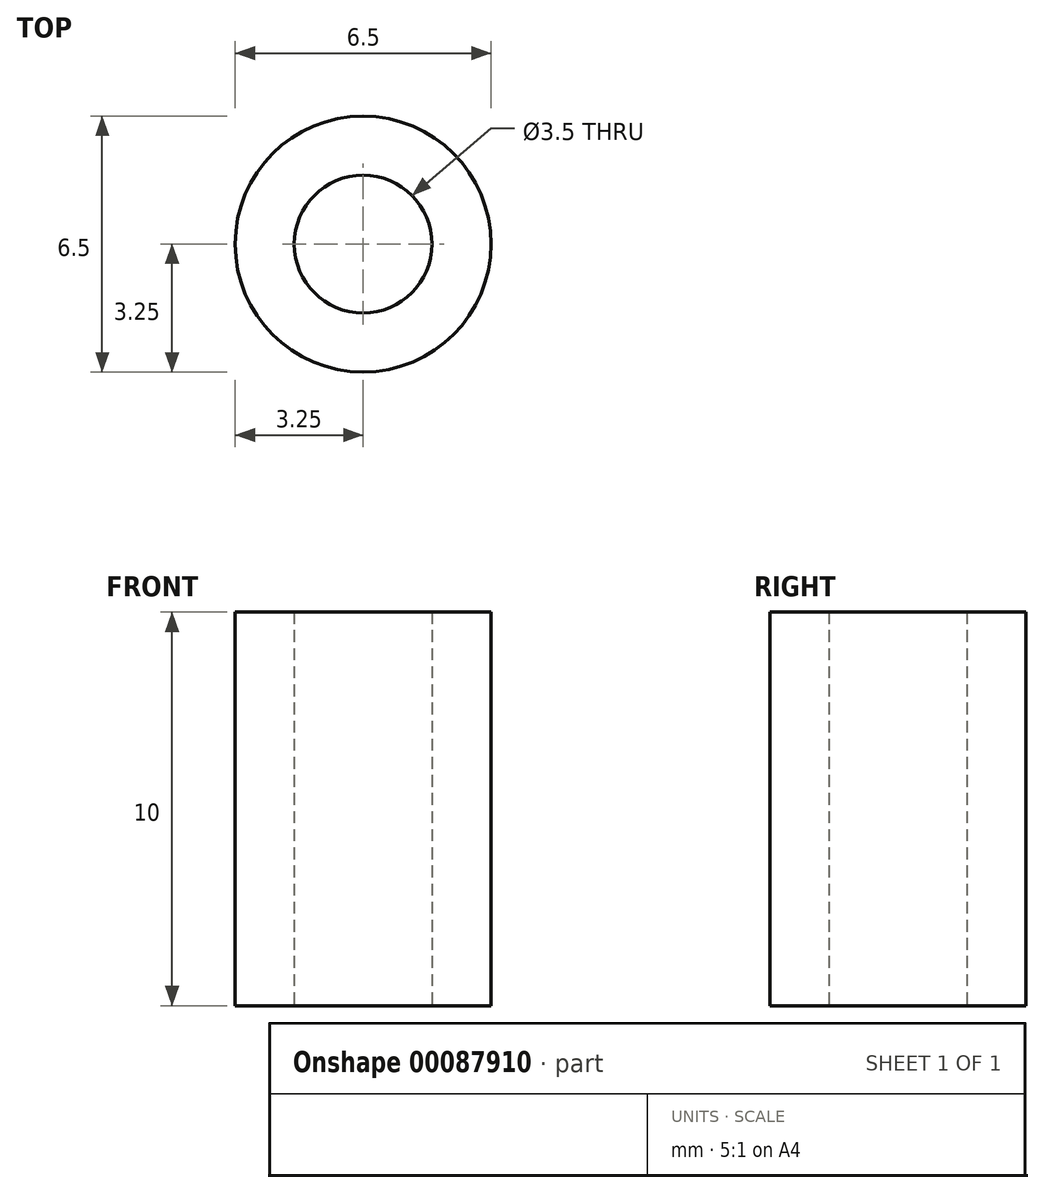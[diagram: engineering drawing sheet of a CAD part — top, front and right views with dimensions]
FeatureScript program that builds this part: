
annotation { "Feature Type Name" : "Feature", "Feature Type Description" : "" }
export const myFeature = defineFeature(function(context is Context, id is Id, definition is map)
    precondition{}
    {
        {
            var Q0;
            Q0=qCreatedBy(makeId("Top.planeOp"),FACE);
            var sketch = newSketch(context, id + "F0", { "sketchPlane" : qUnion([Q0])});
            skCircle(sketch, "E0", {"center": v(0, 0) * mm, "radius": 1.75 * mm});
            skCircle(sketch, "E1", {"center": v(0, 0) * mm, "radius": 3.25 * mm});
            skSolve(sketch);
        }
        {
            var Q0;
            Q0=makeQuery(id+"F0.imprint","IMPRINT",FACE,{"disambiguationData":[TD([[makeQuery(id+"F0.imprint","IMPRINT",EDGE,{"derivedFrom":sQuery(id+"F0.wireOp",EDGE,"E0")}),-1.0]])]});
            extrude(context, id + "F1", {"entities" : qUnion([Q0]), "depth" : 10 * mm});
        }
    });
